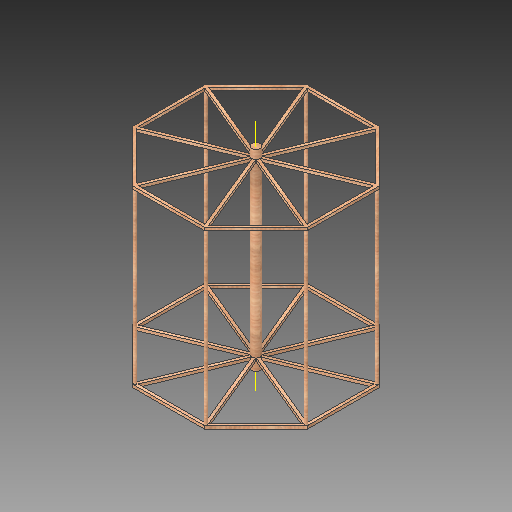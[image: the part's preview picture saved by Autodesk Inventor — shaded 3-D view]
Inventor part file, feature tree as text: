
AUTODESK INVENTOR PART (.ipt)
format: ipt  version: 2019 (Build 230136000, 136)  size: 303,104 bytes
history: native  units: in
note: dims shown in document units (in); Inventor stores cm internally (conversion verified against a paired STEP export)
features: sketch x6, other x4, plane x1
ambient origin geometry x8: Origin, YZ Plane, XZ Plane, XY Plane, X Axis, Y Axis, Z Axis, Center Point
bodies: Solid1 (feature_tree)
feature tree (11):
  other  "RuTAG Roller.ipt"
  other  "Solid1::RuTAG Roller.ipt"
  other  "TaggingFeature1"
  sketch  "Sketch1"  dims[d0=0.3937in]
  sketch  "Sketch2"
  sketch  "Sketch6"
  sketch  "Sketch7"
  sketch  "Sketch8"
  sketch  "Sketch9"
  plane  "Work Plane1"
  other  "Work Axis1"
